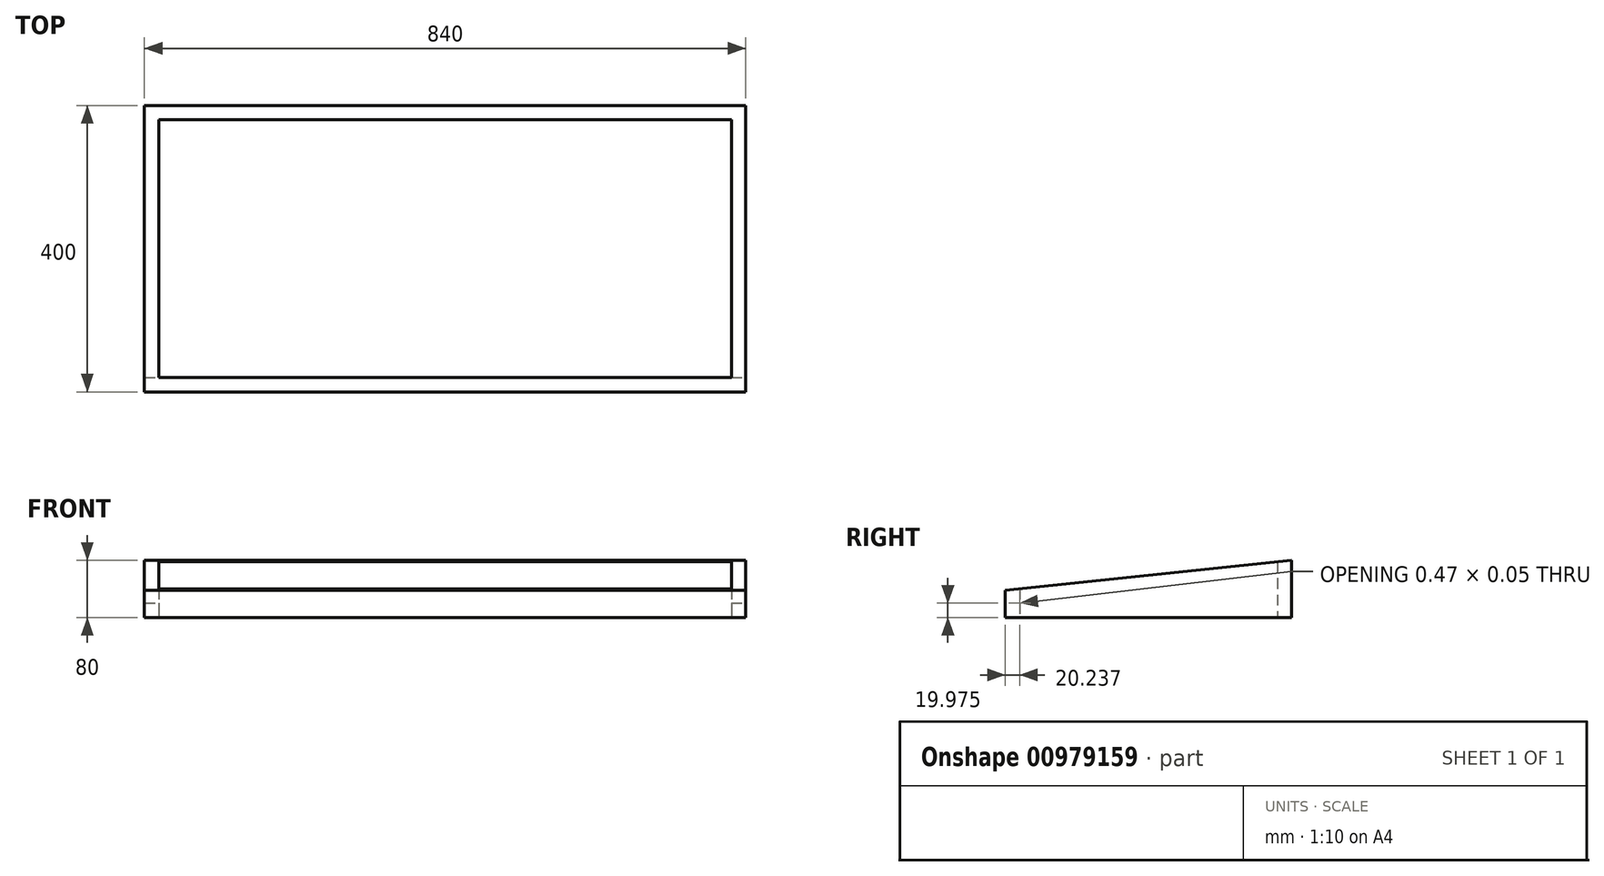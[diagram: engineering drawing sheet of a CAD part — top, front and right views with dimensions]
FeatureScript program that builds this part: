
annotation { "Feature Type Name" : "Feature", "Feature Type Description" : "" }
export const myFeature = defineFeature(function(context is Context, id is Id, definition is map)
    precondition{}
    {
        {
            var Q0;
            Q0=qCreatedBy(makeId("Top.planeOp"),FACE);
            var sketch = newSketch(context, id + "F0", { "sketchPlane" : qUnion([Q0])});
            skLineSegment(sketch, "E0.bottom", {"start": v(-400, 200) * mm, "end": v(400, 200) * mm});
            skLineSegment(sketch, "E0.top", {"start": v(-400, -200) * mm, "end": v(400, -200) * mm});
            skLineSegment(sketch, "E0.left", {"start": v(-400, 200) * mm, "end": v(-400, -200) * mm});
            skLineSegment(sketch, "E0.right", {"start": v(400, 200) * mm, "end": v(400, -200) * mm});
            skPoint(sketch, "E0.middle", {"position": v(0, 0) * mm});
            skSolve(sketch);
        }
        {
            var Q0;
            Q0 = qSketchRegion(id + "F0", true);
            extrude(context, id + "F1", {"entities" : qUnion([Q0]), "endBound" : BoundingType.SYMMETRIC, "depth" : 80 * mm, "offsetDistance" : 25 * mm});
        }
        {
            var Q0;
            Q0=makeQuery(id+"F1.opExtrude","SWEPT_FACE",FACE,{"disambiguationData":[OSD([sQuery(id+"F0.wireOp",EDGE,"E0.right")])]});
            var sketch = newSketch(context, id + "F2", { "sketchPlane" : qUnion([Q0])});
            skLineSegment(sketch, "E1", {"start": v(200, 40) * mm, "end": v(-200, -2.04) * mm});
            skLineSegment(sketch, "E2", {"start": v(-180, -20.05) * mm, "end": v(-180, -20) * mm});
            skLineSegment(sketch, "E3", {"start": v(-180, -20.05) * mm, "end": v(180, 17.79) * mm});
            skLineSegment(sketch, "E4", {"start": v(180, 17.79) * mm, "end": v(180, -20) * mm});
            skLineSegment(sketch, "E5", {"start": v(-180, -20) * mm, "end": v(180, -20) * mm});
            skPoint(sketch, "E6.orphan", {"position": v(180, -40) * mm});
            skCircle(sketch, "E7", {"center": v(104.47, -5.7) * mm, "radius": 10.25 * mm});
            skSolve(sketch);
        }
        {
            var Q0;
            {var subQ0=sQuery(id+"F2.wireOp",EDGE,"E2");Q0=makeQuery(id+"F2.imprint","IMPRINT",FACE,{"disambiguationData":[TD([[makeQuery(id+"F2.imprint","IMPRINT",EDGE,{"derivedFrom":subQ0}),-1.0]])]});}
            var Q1;
            {var subQ0=sQuery(id+"F2.wireOp",EDGE,"E1");Q1=makeQuery(id+"F2.imprint","IMPRINT",FACE,{"disambiguationData":[TD([[makeQuery(id+"F2.imprint","IMPRINT",EDGE,{"derivedFrom":subQ0}),-1.0]])]});}
            extrude(context, id + "F3", {"entities" : qUnion([Q0, Q1]), "operationType" : NewBodyOperationType.REMOVE, "endBound" : BoundingType.THROUGH_ALL, "oppositeDirection" : true, "depth" : 25 * mm, "offsetDistance" : 25 * mm});
        }
        {
            var Q0;
            Q0=makeQuery(id+"F1.opExtrude","SWEPT_FACE",FACE,{"disambiguationData":[OSD([sQuery(id+"F0.wireOp",EDGE,"E0.right")])]});
            var sketch = newSketch(context, id + "F4", { "sketchPlane" : qUnion([Q0])});
            skSolve(sketch);
        }
        {
            var Q0;
            Q0=makeQuery(id+"F4.imprint","IMPRINT",FACE,{"disambiguationData":[TD([[makeQuery(id+"F4.imprint","IMPRINT",EDGE,{"derivedFrom":makeQuery(id+"F3.boolean.opBoolean","COPY",EDGE,{"derivedFrom":makeQuery(id+"F3.opExtrude","CAP_EDGE",EDGE,{"disambiguationData":[OSD([sQuery(id+"F2.wireOp",EDGE,"E2")])],"isStart":true})})}),-1.0]])]});
            var Q1;
            {var subQ0=sQuery(id+"F0.wireOp",EDGE,"E0.right");Q1=makeQuery(id+"F4.imprint","IMPRINT",FACE,{"disambiguationData":[TD([[makeQuery(id+"F4.imprint","IMPRINT",EDGE,{"derivedFrom":makeQuery(id+"F1.opExtrude","CAP_EDGE",EDGE,{"disambiguationData":[OSD([subQ0])],"isStart":true})}),-1.0]])]});}
            extrude(context, id + "F5", {"entities" : qUnion([Q0, Q1]), "depth" : 20 * mm, "offsetDistance" : 25 * mm});
        }
        {
            var Q0;
            Q0=makeQuery(id+"F5.opExtrude","SWEPT_BODY",BODY,{"disambiguationData":[OSD([sQuery(id+"F0.wireOp",EDGE,"E0.bottom"),sQuery(id+"F0.wireOp",EDGE,"E0.top"),sQuery(id+"F0.wireOp",EDGE,"E0.right"),sQuery(id+"F2.wireOp",EDGE,"E1")])]});
            var Q1;
            Q1=qCreatedBy(makeId("Right.planeOp"),FACE);
            mirror(context, id + "F6", {"operationType" : NewBodyOperationType.ADD, "entities" : qUnion([Q0]), "mirrorPlane" : qUnion([Q1])});
        }
        {
            var Q0;
            {var subQ0=sQuery(id+"F0.wireOp",EDGE,"E0.right");var subQ1=makeQuery(id+"F5.opExtrude","SWEPT_FACE",FACE,{"disambiguationData":[OSD([subQ0])]});Q0=makeQuery(id+"F6.boolean.opBoolean","MERGE",FACE,{"derivedFrom":[makeQuery(id+"F1.opExtrude","CAP_FACE",FACE,{"disambiguationData":[OSD([sQuery(id+"F0.wireOp",EDGE,"E0.bottom"),sQuery(id+"F0.wireOp",EDGE,"E0.top"),sQuery(id+"F0.wireOp",EDGE,"E0.left"),subQ0])],"isStart":true}),subQ1,makeQuery(id+"F6.opPattern","COPY",FACE,{"derivedFrom":subQ1,"instanceName":"1"})]});}
            cPlane(context, id + "F7", {"entities" : qUnion([Q0]), "cplaneType" : CPlaneType.OFFSET, "offset" : 20 * mm, "width" : 150 * mm, "height" : 150 * mm});
        }
        {
            var Q0;
            Q0=qCreatedBy(id+"F7.planeOp",FACE);
            var sketch = newSketch(context, id + "F8", { "sketchPlane" : qUnion([Q0])});
            skLineSegment(sketch, "E8.bottom", {"start": v(400, -180) * mm, "end": v(-400, -180) * mm});
            skLineSegment(sketch, "E8.top", {"start": v(400, 180) * mm, "end": v(-400, 180) * mm});
            skLineSegment(sketch, "E8.left", {"start": v(400, -180) * mm, "end": v(400, 180) * mm});
            skLineSegment(sketch, "E8.right", {"start": v(-400, -180) * mm, "end": v(-400, 180) * mm});
            skPoint(sketch, "E8.middle", {"position": v(0, 0) * mm});
            skSolve(sketch);
        }
        {
            var Q0;
            Q0 = qSketchRegion(id + "F8", true);
            extrude(context, id + "F9", {"entities" : qUnion([Q0]), "operationType" : NewBodyOperationType.REMOVE, "endBound" : BoundingType.THROUGH_ALL, "oppositeDirection" : true, "depth" : 25 * mm, "offsetDistance" : 25 * mm});
        }
    });
